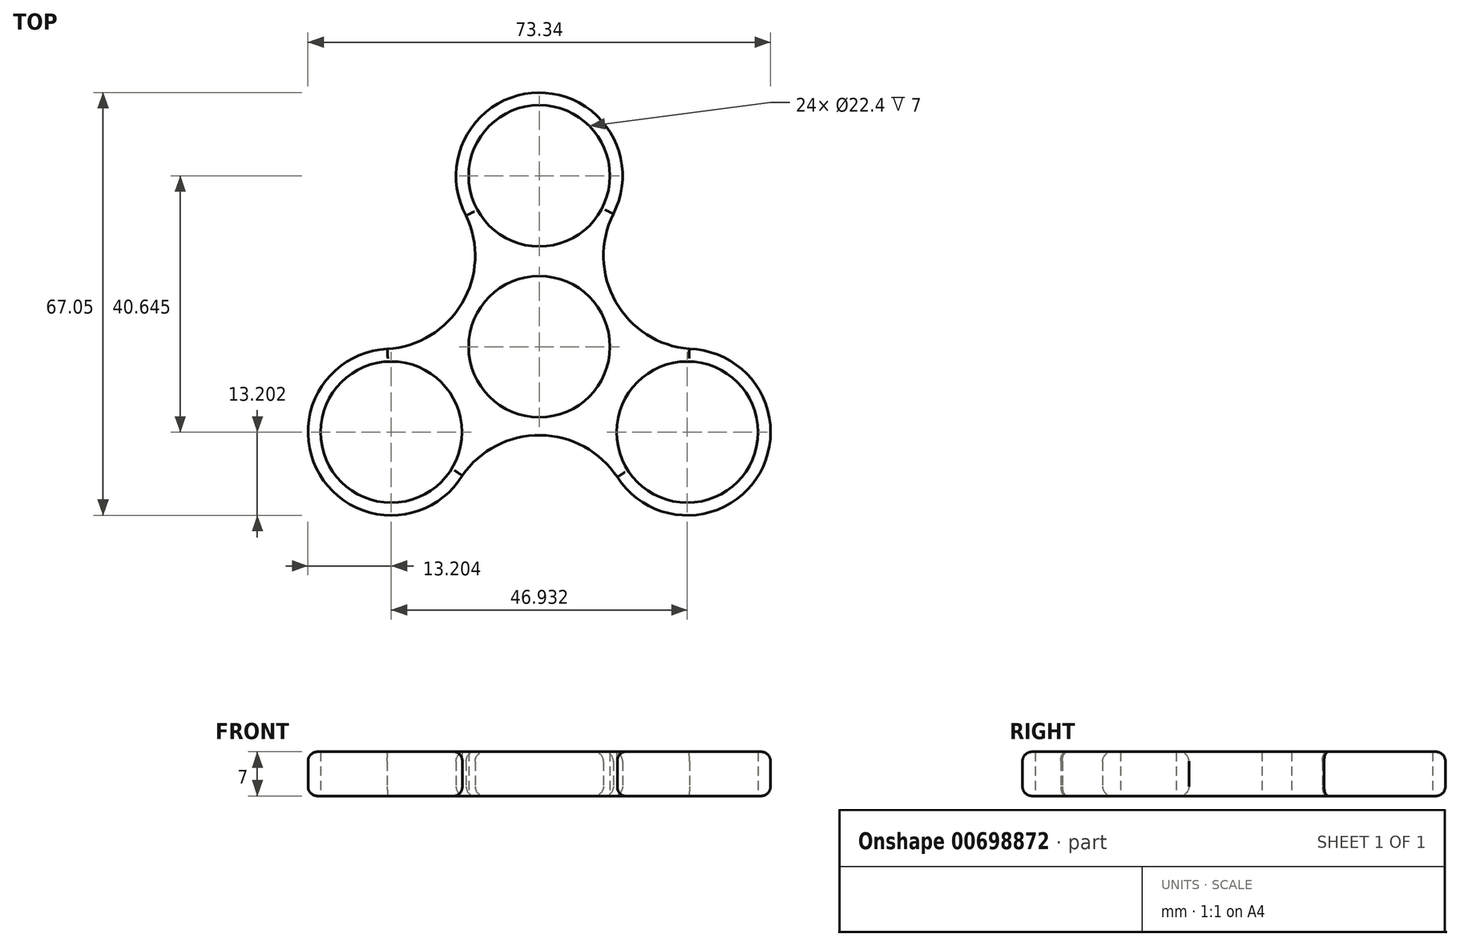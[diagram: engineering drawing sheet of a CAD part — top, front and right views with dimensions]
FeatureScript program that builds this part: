
annotation { "Feature Type Name" : "Feature", "Feature Type Description" : "" }
export const myFeature = defineFeature(function(context is Context, id is Id, definition is map)
    precondition{}
    {
        {
            var Q0;
            Q0=qCreatedBy(makeId("Top.planeOp"),FACE);
            var sketch = newSketch(context, id + "F0", { "sketchPlane" : qUnion([Q0])});
            skCircle(sketch, "E0", {"center": v(0, 0) * mm, "radius": 11.2 * mm});
            skCircle(sketch, "E1", {"center": v(0, 27.1) * mm, "radius": 11.2 * mm});
            skArc(sketch, "E2", {"start": v(11.74, 21.05) * mm, "mid": v(-0.15, 40.3) * mm, "end": v(-11.6, 20.78) * mm});
            skArc(sketch, "E3.1.0", {"start": v(-24.1, -0.36) * mm, "mid": v(-34.82, -20.28) * mm, "end": v(-12.2, -20.43) * mm});
            skCircle(sketch, "E3.1.1", {"center": v(-23.47, -13.55) * mm, "radius": 11.2 * mm});
            skArc(sketch, "E3.2.0", {"start": v(12.37, -20.7) * mm, "mid": v(34.97, -20.02) * mm, "end": v(23.8, -0.35) * mm});
            skCircle(sketch, "E3.2.1", {"center": v(23.47, -13.55) * mm, "radius": 11.2 * mm});
            skArc(sketch, "E4", {"start": v(11.74, 21.05) * mm, "mid": v(12.28, 6.8) * mm, "end": v(24.59, -0.4) * mm});
            skArc(sketch, "E5.1.0", {"start": v(-24.1, -0.36) * mm, "mid": v(-12.04, 7.24) * mm, "end": v(-11.95, 21.5) * mm});
            skArc(sketch, "E5.2.0", {"start": v(12.37, -20.7) * mm, "mid": v(-0.25, -14.04) * mm, "end": v(-12.64, -21.1) * mm});
            skSolve(sketch);
        }
        {
            var Q0;
            Q0 = qSketchRegion(id + "F0", true);
            extrude(context, id + "F1", {"entities" : qUnion([Q0]), "depth" : 7 * mm, "offsetDistance" : 25 * mm});
        }
        {
            var Q0;
            Q0=makeQuery(id+"F1.opExtrude","CAP_EDGE",EDGE,{"disambiguationData":[OSD([sQuery(id+"F0.wireOp",EDGE,"E5.1.0")])],"isStart":true});
            var Q1;
            Q1=makeQuery(id+"F1.opExtrude","CAP_EDGE",EDGE,{"disambiguationData":[OSD([sQuery(id+"F0.wireOp",EDGE,"E2")])],"isStart":true});
            var Q2;
            Q2=makeQuery(id+"F1.opExtrude","CAP_EDGE",EDGE,{"disambiguationData":[OSD([sQuery(id+"F0.wireOp",EDGE,"E4")])],"isStart":true});
            var Q3;
            Q3=makeQuery(id+"F1.opExtrude","CAP_EDGE",EDGE,{"disambiguationData":[OSD([sQuery(id+"F0.wireOp",EDGE,"E3.2.0")])],"isStart":true});
            var Q4;
            Q4=makeQuery(id+"F1.opExtrude","CAP_EDGE",EDGE,{"disambiguationData":[OSD([sQuery(id+"F0.wireOp",EDGE,"E5.2.0")])],"isStart":true});
            var Q5;
            Q5=makeQuery(id+"F1.opExtrude","CAP_EDGE",EDGE,{"disambiguationData":[OSD([sQuery(id+"F0.wireOp",EDGE,"E3.1.0")])],"isStart":true});
            var Q6;
            Q6=makeQuery(id+"F1.opExtrude","CAP_EDGE",EDGE,{"disambiguationData":[OSD([sQuery(id+"F0.wireOp",EDGE,"E3.2.0")])],"isStart":false});
            var Q7;
            Q7=makeQuery(id+"F1.opExtrude","CAP_EDGE",EDGE,{"disambiguationData":[OSD([sQuery(id+"F0.wireOp",EDGE,"E4")])],"isStart":false});
            var Q8;
            Q8=makeQuery(id+"F1.opExtrude","CAP_EDGE",EDGE,{"disambiguationData":[OSD([sQuery(id+"F0.wireOp",EDGE,"E2")])],"isStart":false});
            var Q9;
            Q9=makeQuery(id+"F1.opExtrude","CAP_EDGE",EDGE,{"disambiguationData":[OSD([sQuery(id+"F0.wireOp",EDGE,"E5.1.0")])],"isStart":false});
            var Q10;
            Q10=makeQuery(id+"F1.opExtrude","CAP_EDGE",EDGE,{"disambiguationData":[OSD([sQuery(id+"F0.wireOp",EDGE,"E3.1.0")])],"isStart":false});
            var Q11;
            Q11=makeQuery(id+"F1.opExtrude","CAP_EDGE",EDGE,{"disambiguationData":[OSD([sQuery(id+"F0.wireOp",EDGE,"E5.2.0")])],"isStart":false});
            fillet(context, id + "F2", {"entities" : qUnion([Q0, Q1, Q2, Q3, Q4, Q5, Q6, Q7, Q8, Q9, Q10, Q11]), "radius" : 1.5 * mm, "tangentPropagation" : true, "allowEdgeOverflow" : false});
        }
    });
